# Revit family: BIMLIB_Конвектор_МебельныйЭлектрический_ВКВМЭ090_VITRON
name_source: partatom
category: Оборудование
revit_build: Autodesk Revit 2017 (Build: 20190508_0315(x64)
units: mm (PartAtom-declared; Revit-internal decimal feet)

## family parameters
Всегда вертикально = Да
На основе рабочей плоскости = Нет
Общий = Нет
При загрузке вырезать с полостями = Нет
Размер круглого соединителя = Использовать диаметр
Тип детали = Нормальный
Точка расчета площади = Нет

## types (1)
- Конвектор_Шириной 335мм
    1 = 1
    2 = 2
    3 = 3
    ADSK_URL документации изделия = https://vitron.ru
    ADSK_URL страницы изделия = https://vitron.ru
    ADSK_Версия Revit = 2017
    ADSK_Единица измерения = шт.
    ADSK_Завод-изготовитель = Вилма / VITRON
    ADSK_Классификация нагрузок = Прочее
    ADSK_Количество фаз = 1
    ADSK_Коэффициент мощности = 0.98
    ADSK_Обозначение = ВКВМЭ90.335
    ADSK_Размер_Высота = 90 мм
    ADSK_Размер_Диаметр = 15 мм
    ADSK_Размер_Ширина = 335 мм
    BL_BIM library = https://bimlib.pro
    URL = https://vitron.ru
    VIT_Степень защиты вентилятора = IP20
    VIT_Тепловая мощность на 1 м = 1000 Вт
    VIT_Уровень звукового давления от вентилятора = 19/30 дБ(А)
    Изготовитель = Вилма / VITRON
    Материал_Корпуса = BIMLIB_ОцинкованнаяСтальЧерная_VITRON
    Материал_Решетка = BIMLIB_Алюминий_VITRON
    Описание = Встраиваемый под мебель (например, кухонные гарнитуры) электрический конвектор отопления с принудительной конвекцией VITRON . Состоит из корпуса, вентилятора , декоративной решетки и нагревательного элемента, в качестве которого используется терморезистор. 
Данный тип конвекторов предназначены для использования как вспомогательные отопительные приборы с системами водяного отопления, системами теплого пола, так и в качестве основного источника тепла, в местах где нет возможности использовать системы водяного отопления. Служит для отопления сухих помещений 
       Основное преимущество электрических конвекторов отсутствие необходимости в прокладке трубопровода. Так же преимущество в более высокой теплоотдаче в сравнении с аналогичными моделями с водяным теплообменником.
